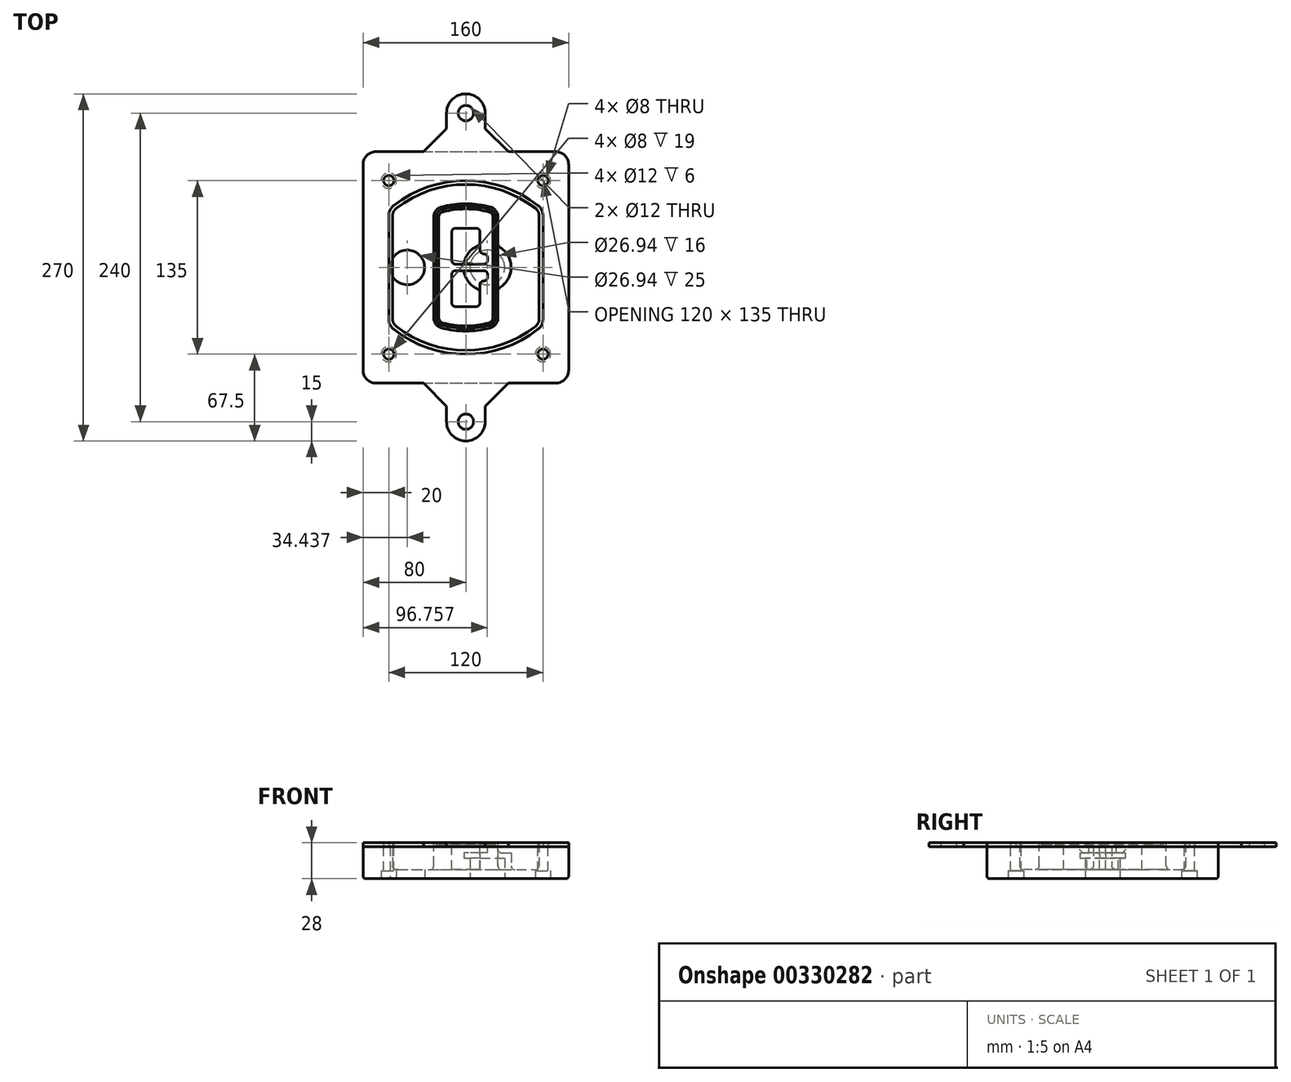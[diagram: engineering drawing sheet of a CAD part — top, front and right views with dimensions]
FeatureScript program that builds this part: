
annotation { "Feature Type Name" : "Feature", "Feature Type Description" : "" }
export const myFeature = defineFeature(function(context is Context, id is Id, definition is map)
    precondition{}
    {
        {
            var Q0;
            Q0=qCreatedBy(makeId("Top.planeOp"),FACE);
            var sketch = newSketch(context, id + "F0", { "sketchPlane" : qUnion([Q0])});
            skPoint(sketch, "E0.rect.middle", {"position": v(0, 0) * mm});
            skLineSegment(sketch, "E1.bottom", {"start": v(-70, -90) * mm, "end": v(70, -90) * mm});
            skLineSegment(sketch, "E1.top", {"start": v(-70, 90) * mm, "end": v(70, 90) * mm});
            skLineSegment(sketch, "E1.left", {"start": v(-80, -80) * mm, "end": v(-80, 80) * mm});
            skLineSegment(sketch, "E1.right", {"start": v(80, -80) * mm, "end": v(80, 80) * mm});
            skLineSegment(sketch, "E2", {"start": v(-80, 90) * mm, "end": v(80, -90) * mm, "construction": true});
            skLineSegment(sketch, "E3", {"start": v(80, 90) * mm, "end": v(-80, -90) * mm, "construction": true});
            skCircle(sketch, "E4", {"center": v(-60, 67.5) * mm, "radius": 4 * mm});
            skCircle(sketch, "E5", {"center": v(60, 67.5) * mm, "radius": 4 * mm});
            skCircle(sketch, "E6", {"center": v(60, -67.5) * mm, "radius": 4 * mm});
            skCircle(sketch, "E7", {"center": v(-60, -67.5) * mm, "radius": 4 * mm});
            skLineSegment(sketch, "E8", {"start": v(-60, 67.5) * mm, "end": v(60, 67.5) * mm, "construction": true});
            skLineSegment(sketch, "E9", {"start": v(60, 67.5) * mm, "end": v(60, -67.5) * mm, "construction": true});
            skLineSegment(sketch, "E10", {"start": v(60, -67.5) * mm, "end": v(-60, -67.5) * mm, "construction": true});
            skLineSegment(sketch, "E11", {"start": v(-60, -67.5) * mm, "end": v(-60, 67.5) * mm, "construction": true});
            skLineSegment(sketch, "E12", {"start": v(-60, 40.3) * mm, "end": v(-60, -40.3) * mm});
            skLineSegment(sketch, "E13", {"start": v(60, 40.3) * mm, "end": v(60, -40.3) * mm});
            skArc(sketch, "E14", {"start": v(56.15, 48.18) * mm, "mid": v(0, 67.5) * mm, "end": v(-56.15, 48.18) * mm});
            skArc(sketch, "E15", {"start": v(-56.15, -48.18) * mm, "mid": v(0, -67.5) * mm, "end": v(56.15, -48.18) * mm});
            skLineSegment(sketch, "E16", {"start": v(-60, 0) * mm, "end": v(60, 0) * mm, "construction": true});
            skPoint(sketch, "E17.visualSharp", {"position": v(-60, -45) * mm});
            skArc(sketch, "E17.filletArc", {"start": v(-60, -40.3) * mm, "mid": v(-58.99, -44.68) * mm, "end": v(-56.15, -48.18) * mm});
            skPoint(sketch, "E18.visualSharp", {"position": v(-60, 45) * mm});
            skArc(sketch, "E18.filletArc", {"start": v(-56.15, 48.18) * mm, "mid": v(-58.99, 44.68) * mm, "end": v(-60, 40.3) * mm});
            skPoint(sketch, "E19.visualSharp", {"position": v(60, 45) * mm});
            skArc(sketch, "E19.filletArc", {"start": v(60, 40.3) * mm, "mid": v(58.99, 44.68) * mm, "end": v(56.15, 48.18) * mm});
            skPoint(sketch, "E20.visualSharp", {"position": v(60, -45) * mm});
            skArc(sketch, "E20.filletArc", {"start": v(56.15, -48.18) * mm, "mid": v(58.99, -44.68) * mm, "end": v(60, -40.3) * mm});
            skPoint(sketch, "E21.visualSharp", {"position": v(-80, 90) * mm});
            skArc(sketch, "E21.filletArc", {"start": v(-70, 90) * mm, "mid": v(-77.07, 87.07) * mm, "end": v(-80, 80) * mm});
            skPoint(sketch, "E22.visualSharp", {"position": v(80, 90) * mm});
            skArc(sketch, "E22.filletArc", {"start": v(80, 80) * mm, "mid": v(77.07, 87.07) * mm, "end": v(70, 90) * mm});
            skPoint(sketch, "E23.visualSharp", {"position": v(80, -90) * mm});
            skArc(sketch, "E23.filletArc", {"start": v(70, -90) * mm, "mid": v(77.07, -87.07) * mm, "end": v(80, -80) * mm});
            skPoint(sketch, "E24.visualSharp", {"position": v(-80, -90) * mm});
            skArc(sketch, "E24.filletArc", {"start": v(-80, -80) * mm, "mid": v(-77.07, -87.07) * mm, "end": v(-70, -90) * mm});
            skArc(sketch, "E25.0", {"start": v(57, 40.3) * mm, "mid": v(56.3, 43.36) * mm, "end": v(54.3, 45.81) * mm});
            skLineSegment(sketch, "E25.1", {"start": v(57, 40.3) * mm, "end": v(57, -40.3) * mm});
            skArc(sketch, "E25.2", {"start": v(54.3, -45.81) * mm, "mid": v(56.3, -43.36) * mm, "end": v(57, -40.3) * mm});
            skArc(sketch, "E25.3", {"start": v(-54.3, -45.81) * mm, "mid": v(0, -64.5) * mm, "end": v(54.3, -45.81) * mm});
            skArc(sketch, "E25.4", {"start": v(-57, -40.3) * mm, "mid": v(-56.3, -43.36) * mm, "end": v(-54.3, -45.81) * mm});
            skArc(sketch, "E25.5", {"start": v(54.3, 45.81) * mm, "mid": v(0, 64.5) * mm, "end": v(-54.3, 45.81) * mm});
            skLineSegment(sketch, "E25.6", {"start": v(-57, 40.3) * mm, "end": v(-57, -40.3) * mm});
            skArc(sketch, "E25.7", {"start": v(-54.3, 45.81) * mm, "mid": v(-56.3, 43.36) * mm, "end": v(-57, 40.3) * mm});
            skArc(sketch, "E26.0", {"start": v(-58.62, 51.33) * mm, "mid": v(-62.58, 46.43) * mm, "end": v(-64, 40.3) * mm});
            skArc(sketch, "E26.1", {"start": v(58.62, 51.33) * mm, "mid": v(0, 71.5) * mm, "end": v(-58.62, 51.33) * mm});
            skArc(sketch, "E26.2", {"start": v(64, 40.3) * mm, "mid": v(62.58, 46.43) * mm, "end": v(58.62, 51.33) * mm});
            skLineSegment(sketch, "E26.3", {"start": v(64, 40.3) * mm, "end": v(64, -40.3) * mm});
            skArc(sketch, "E26.4", {"start": v(58.62, -51.33) * mm, "mid": v(62.58, -46.43) * mm, "end": v(64, -40.3) * mm});
            skLineSegment(sketch, "E26.5", {"start": v(-64, 40.3) * mm, "end": v(-64, -40.3) * mm});
            skArc(sketch, "E26.6", {"start": v(-58.62, -51.33) * mm, "mid": v(0, -71.5) * mm, "end": v(58.62, -51.33) * mm});
            skArc(sketch, "E26.7", {"start": v(-64, -40.3) * mm, "mid": v(-62.58, -46.43) * mm, "end": v(-58.62, -51.33) * mm});
            skSolve(sketch);
        }
        {
            var Q0;
            Q0=makeQuery(id+"F0.imprint","IMPRINT",FACE,{"disambiguationData":[TD([[makeQuery(id+"F0.imprint","IMPRINT",EDGE,{"derivedFrom":sQuery(id+"F0.wireOp",EDGE,"E1.bottom")}),1.0]])]});
            var Q1;
            Q1=makeQuery(id+"F0.imprint","IMPRINT",FACE,{"disambiguationData":[TD([[makeQuery(id+"F0.imprint","IMPRINT",EDGE,{"derivedFrom":sQuery(id+"F0.wireOp",EDGE,"E12")}),1.0]])]});
            var Q2;
            Q2=makeQuery(id+"F0.imprint","IMPRINT",FACE,{"disambiguationData":[TD([[makeQuery(id+"F0.imprint","IMPRINT",EDGE,{"derivedFrom":sQuery(id+"F0.wireOp",EDGE,"E25.0")}),1.0]])]});
            var Q3;
            Q3=makeQuery(id+"F0.imprint","IMPRINT",FACE,{"disambiguationData":[TD([[makeQuery(id+"F0.imprint","IMPRINT",EDGE,{"derivedFrom":sQuery(id+"F0.wireOp",EDGE,"E12")}),-1.0]])]});
            extrude(context, id + "F1", {"entities" : qUnion([Q0, Q1, Q2, Q3]), "oppositeDirection" : true, "depth" : 25 * mm});
        }
        {
            var Q0;
            Q0=makeQuery(id+"F0.imprint","IMPRINT",FACE,{"disambiguationData":[TD([[makeQuery(id+"F0.imprint","IMPRINT",EDGE,{"derivedFrom":sQuery(id+"F0.wireOp",EDGE,"E12")}),1.0]])]});
            extrude(context, id + "F2", {"entities" : qUnion([Q0]), "operationType" : NewBodyOperationType.ADD, "depth" : 3 * mm});
        }
        {
            var Q0;
            Q0=makeQuery(id+"F0.imprint","IMPRINT",FACE,{"disambiguationData":[TD([[makeQuery(id+"F0.imprint","IMPRINT",EDGE,{"derivedFrom":sQuery(id+"F0.wireOp",EDGE,"E25.0")}),1.0]])]});
            extrude(context, id + "F3", {"entities" : qUnion([Q0]), "operationType" : NewBodyOperationType.REMOVE, "oppositeDirection" : true, "depth" : 18 * mm});
        }
        {
            var Q0;
            Q0=makeQuery(id+"F2.opExtrude","CAP_FACE",FACE,{"disambiguationData":[OSD([sQuery(id+"F0.wireOp",EDGE,"E12"),sQuery(id+"F0.wireOp",EDGE,"E13"),sQuery(id+"F0.wireOp",EDGE,"E14"),sQuery(id+"F0.wireOp",EDGE,"E15"),sQuery(id+"F0.wireOp",EDGE,"E17.filletArc"),sQuery(id+"F0.wireOp",EDGE,"E18.filletArc"),sQuery(id+"F0.wireOp",EDGE,"E19.filletArc"),sQuery(id+"F0.wireOp",EDGE,"E20.filletArc"),sQuery(id+"F0.wireOp",EDGE,"E25.0"),sQuery(id+"F0.wireOp",EDGE,"E25.1"),sQuery(id+"F0.wireOp",EDGE,"E25.2"),sQuery(id+"F0.wireOp",EDGE,"E25.3"),sQuery(id+"F0.wireOp",EDGE,"E25.4"),sQuery(id+"F0.wireOp",EDGE,"E25.5"),sQuery(id+"F0.wireOp",EDGE,"E25.6"),sQuery(id+"F0.wireOp",EDGE,"E25.7")])],"isStart":false});
            var sketch = newSketch(context, id + "F4", { "sketchPlane" : qUnion([Q0])});
            skArc(sketch, "E27.0", {"start": v(-19.08, -46.97) * mm, "mid": v(0, -49.5) * mm, "end": v(19.08, -46.97) * mm});
            skArc(sketch, "E28.0", {"start": v(19.08, 46.97) * mm, "mid": v(0, 49.5) * mm, "end": v(-19.08, 46.97) * mm});
            skLineSegment(sketch, "E29", {"start": v(-25, 39.25) * mm, "end": v(-25, -39.25) * mm});
            skLineSegment(sketch, "E30", {"start": v(25, 39.25) * mm, "end": v(25, -39.25) * mm});
            skLineSegment(sketch, "E31", {"start": v(-25, 45.1) * mm, "end": v(25, 45.1) * mm, "construction": true});
            skLineSegment(sketch, "E32", {"start": v(-25, -45.1) * mm, "end": v(25, -45.1) * mm, "construction": true});
            skPoint(sketch, "E33.visualSharp", {"position": v(-25, 45.1) * mm});
            skArc(sketch, "E33.filletArc", {"start": v(-19.08, 46.97) * mm, "mid": v(-23.35, 44.11) * mm, "end": v(-25, 39.25) * mm});
            skPoint(sketch, "E34.visualSharp", {"position": v(25, 45.1) * mm});
            skArc(sketch, "E34.filletArc", {"start": v(25, 39.25) * mm, "mid": v(23.35, 44.11) * mm, "end": v(19.08, 46.97) * mm});
            skPoint(sketch, "E35.visualSharp", {"position": v(25, -45.1) * mm});
            skArc(sketch, "E35.filletArc", {"start": v(19.08, -46.97) * mm, "mid": v(23.35, -44.11) * mm, "end": v(25, -39.25) * mm});
            skPoint(sketch, "E36.visualSharp", {"position": v(-25, -45.1) * mm});
            skArc(sketch, "E36.filletArc", {"start": v(-25, -39.25) * mm, "mid": v(-23.35, -44.11) * mm, "end": v(-19.08, -46.97) * mm});
            skArc(sketch, "E37.0", {"start": v(54.3, 45.81) * mm, "mid": v(0, 64.5) * mm, "end": v(-54.3, 45.81) * mm});
            skArc(sketch, "E37.1", {"start": v(-54.3, 45.81) * mm, "mid": v(-56.3, 43.36) * mm, "end": v(-57, 40.3) * mm});
            skLineSegment(sketch, "E37.2", {"start": v(-57, 40.3) * mm, "end": v(-57, -40.3) * mm});
            skArc(sketch, "E37.3", {"start": v(-57, -40.3) * mm, "mid": v(-56.3, -43.36) * mm, "end": v(-54.3, -45.81) * mm});
            skArc(sketch, "E37.4", {"start": v(-54.3, -45.81) * mm, "mid": v(0, -64.5) * mm, "end": v(54.3, -45.81) * mm});
            skArc(sketch, "E37.5", {"start": v(54.3, -45.81) * mm, "mid": v(56.3, -43.36) * mm, "end": v(57, -40.3) * mm});
            skLineSegment(sketch, "E37.6", {"start": v(57, 40.3) * mm, "end": v(57, -40.3) * mm});
            skArc(sketch, "E37.7", {"start": v(57, 40.3) * mm, "mid": v(56.3, 43.36) * mm, "end": v(54.3, 45.81) * mm});
            skLineSegment(sketch, "E38.0", {"start": v(23, 39.25) * mm, "end": v(23, -39.25) * mm});
            skArc(sketch, "E38.1", {"start": v(18.56, -45.04) * mm, "mid": v(21.76, -42.9) * mm, "end": v(23, -39.25) * mm});
            skArc(sketch, "E38.2", {"start": v(-18.56, -45.04) * mm, "mid": v(0, -47.5) * mm, "end": v(18.56, -45.04) * mm});
            skArc(sketch, "E38.3", {"start": v(-23, -39.25) * mm, "mid": v(-21.76, -42.9) * mm, "end": v(-18.56, -45.04) * mm});
            skLineSegment(sketch, "E38.4", {"start": v(-23, 39.25) * mm, "end": v(-23, -39.25) * mm});
            skArc(sketch, "E38.5", {"start": v(23, 39.25) * mm, "mid": v(21.76, 42.9) * mm, "end": v(18.56, 45.04) * mm});
            skArc(sketch, "E38.6", {"start": v(-18.56, 45.04) * mm, "mid": v(-21.76, 42.9) * mm, "end": v(-23, 39.25) * mm});
            skArc(sketch, "E38.7", {"start": v(18.56, 45.04) * mm, "mid": v(0, 47.5) * mm, "end": v(-18.56, 45.04) * mm});
            skArc(sketch, "E39.0", {"start": v(21, 39.25) * mm, "mid": v(20.18, 41.68) * mm, "end": v(18.04, 43.1) * mm});
            skLineSegment(sketch, "E39.1", {"start": v(21, 39.25) * mm, "end": v(21, -39.25) * mm});
            skArc(sketch, "E39.2", {"start": v(18.04, -43.1) * mm, "mid": v(20.18, -41.68) * mm, "end": v(21, -39.25) * mm});
            skArc(sketch, "E39.3", {"start": v(-18.04, -43.1) * mm, "mid": v(0, -45.5) * mm, "end": v(18.04, -43.1) * mm});
            skArc(sketch, "E39.4", {"start": v(-21, -39.25) * mm, "mid": v(-20.18, -41.68) * mm, "end": v(-18.04, -43.1) * mm});
            skArc(sketch, "E39.5", {"start": v(18.04, 43.1) * mm, "mid": v(0, 45.5) * mm, "end": v(-18.04, 43.1) * mm});
            skLineSegment(sketch, "E39.6", {"start": v(-21, 39.25) * mm, "end": v(-21, -39.25) * mm});
            skArc(sketch, "E39.7", {"start": v(-18.04, 43.1) * mm, "mid": v(-20.18, 41.68) * mm, "end": v(-21, 39.25) * mm});
            skLineSegment(sketch, "E40", {"start": v(-25, 0) * mm, "end": v(25, 0) * mm, "construction": true});
            skLineSegment(sketch, "E41", {"start": v(-11, 5.5) * mm, "end": v(-11, 27.5) * mm});
            skLineSegment(sketch, "E42", {"start": v(-8, 30.5) * mm, "end": v(8, 30.5) * mm});
            skLineSegment(sketch, "E43", {"start": v(11, 27.5) * mm, "end": v(11, 13.5) * mm});
            skLineSegment(sketch, "E44", {"start": v(14, 10.5) * mm, "end": v(14, 10.5) * mm});
            skLineSegment(sketch, "E45", {"start": v(17, 7.5) * mm, "end": v(17, 5.5) * mm});
            skLineSegment(sketch, "E46", {"start": v(14, 2.5) * mm, "end": v(-8, 2.5) * mm});
            skPoint(sketch, "E47.visualSharp", {"position": v(-11, 30.5) * mm});
            skArc(sketch, "E47.filletArc", {"start": v(-8, 30.5) * mm, "mid": v(-10.12, 29.62) * mm, "end": v(-11, 27.5) * mm});
            skPoint(sketch, "E48.visualSharp", {"position": v(11, 30.5) * mm});
            skArc(sketch, "E48.filletArc", {"start": v(11, 27.5) * mm, "mid": v(10.12, 29.62) * mm, "end": v(8, 30.5) * mm});
            skPoint(sketch, "E49.visualSharp", {"position": v(11, 10.5) * mm});
            skArc(sketch, "E49.filletArc", {"start": v(11, 13.5) * mm, "mid": v(11.88, 11.38) * mm, "end": v(14, 10.5) * mm});
            skPoint(sketch, "E50.visualSharp", {"position": v(17, 10.5) * mm});
            skArc(sketch, "E50.filletArc", {"start": v(17, 7.5) * mm, "mid": v(16.12, 9.62) * mm, "end": v(14, 10.5) * mm});
            skPoint(sketch, "E51.visualSharp", {"position": v(17, 2.5) * mm});
            skArc(sketch, "E51.filletArc", {"start": v(14, 2.5) * mm, "mid": v(16.12, 3.38) * mm, "end": v(17, 5.5) * mm});
            skPoint(sketch, "E52.visualSharp", {"position": v(-11, 2.5) * mm});
            skArc(sketch, "E52.filletArc", {"start": v(-11, 5.5) * mm, "mid": v(-10.12, 3.38) * mm, "end": v(-8, 2.5) * mm});
            skLineSegment(sketch, "E53.0.MirrorCS", {"start": v(14, -2.5) * mm, "end": v(-8, -2.5) * mm});
            skArc(sketch, "E54.0.MirrorCS", {"start": v(-11, -5.5) * mm, "mid": v(-10.12, -3.38) * mm, "end": v(-8, -2.5) * mm});
            skLineSegment(sketch, "E55.0.MirrorCS", {"start": v(-11, -5.5) * mm, "end": v(-11, -27.5) * mm});
            skArc(sketch, "E56.0.MirrorCS", {"start": v(-8, -30.5) * mm, "mid": v(-10.12, -29.62) * mm, "end": v(-11, -27.5) * mm});
            skLineSegment(sketch, "E57.0.MirrorCS", {"start": v(-8, -30.5) * mm, "end": v(8, -30.5) * mm});
            skArc(sketch, "E58.0.MirrorCS", {"start": v(11, -27.5) * mm, "mid": v(10.12, -29.62) * mm, "end": v(8, -30.5) * mm});
            skLineSegment(sketch, "E59.0.MirrorCS", {"start": v(11, -27.5) * mm, "end": v(11, -13.5) * mm});
            skArc(sketch, "E60.0.MirrorCS", {"start": v(11, -13.5) * mm, "mid": v(11.88, -11.38) * mm, "end": v(14, -10.5) * mm});
            skArc(sketch, "E61.0.MirrorCS", {"start": v(17, -7.5) * mm, "mid": v(16.12, -9.62) * mm, "end": v(14, -10.5) * mm});
            skLineSegment(sketch, "E62.0.MirrorCS", {"start": v(17, -7.5) * mm, "end": v(17, -5.5) * mm});
            skArc(sketch, "E63.0.MirrorCS", {"start": v(14, -2.5) * mm, "mid": v(16.12, -3.38) * mm, "end": v(17, -5.5) * mm});
            skSolve(sketch);
        }
        {
            var Q0;
            Q0=makeQuery(id+"F4.imprint","IMPRINT",FACE,{"disambiguationData":[TD([[makeQuery(id+"F4.imprint","IMPRINT",EDGE,{"derivedFrom":sQuery(id+"F4.wireOp",EDGE,"E27.0")}),1.0]])]});
            var Q1;
            Q1=makeQuery(id+"F4.imprint","IMPRINT",FACE,{"disambiguationData":[TD([[makeQuery(id+"F4.imprint","IMPRINT",EDGE,{"derivedFrom":sQuery(id+"F4.wireOp",EDGE,"E38.0")}),-1.0]])]});
            var Q2;
            Q2=makeQuery(id+"F4.imprint","IMPRINT",FACE,{"disambiguationData":[TD([[makeQuery(id+"F4.imprint","IMPRINT",EDGE,{"derivedFrom":sQuery(id+"F4.wireOp",EDGE,"E39.0")}),1.0]])]});
            extrude(context, id + "F5", {"entities" : qUnion([Q0, Q1, Q2]), "operationType" : NewBodyOperationType.ADD, "endBound" : BoundingType.UP_TO_NEXT, "oppositeDirection" : true, "depth" : 25 * mm});
        }
        {
            var Q0;
            Q0=makeQuery(id+"F4.imprint","IMPRINT",FACE,{"disambiguationData":[TD([[makeQuery(id+"F4.imprint","IMPRINT",EDGE,{"derivedFrom":sQuery(id+"F4.wireOp",EDGE,"E38.0")}),-1.0]])]});
            extrude(context, id + "F6", {"entities" : qUnion([Q0]), "operationType" : NewBodyOperationType.REMOVE, "oppositeDirection" : true, "depth" : 2 * mm});
        }
        {
            var Q0;
            Q0=makeQuery(id+"F1.opExtrude","CAP_FACE",FACE,{"disambiguationData":[OSD([sQuery(id+"F0.wireOp",EDGE,"E1.bottom"),sQuery(id+"F0.wireOp",EDGE,"E1.top"),sQuery(id+"F0.wireOp",EDGE,"E1.left"),sQuery(id+"F0.wireOp",EDGE,"E1.right"),sQuery(id+"F0.wireOp",EDGE,"E4"),sQuery(id+"F0.wireOp",EDGE,"E5"),sQuery(id+"F0.wireOp",EDGE,"E6"),sQuery(id+"F0.wireOp",EDGE,"E7"),sQuery(id+"F0.wireOp",EDGE,"E21.filletArc"),sQuery(id+"F0.wireOp",EDGE,"E22.filletArc"),sQuery(id+"F0.wireOp",EDGE,"E23.filletArc"),sQuery(id+"F0.wireOp",EDGE,"E24.filletArc")])],"isStart":false});
            var sketch = newSketch(context, id + "F7", { "sketchPlane" : qUnion([Q0])});
            skCircle(sketch, "E64", {"center": v(16.76, 0) * mm, "radius": 13.47 * mm});
            skCircle(sketch, "E65", {"center": v(-45.56, 0) * mm, "radius": 13.47 * mm});
            skLineSegment(sketch, "E66", {"start": v(80, 0) * mm, "end": v(-80, 0) * mm});
            skCircle(sketch, "E67", {"center": v(16.76, 0) * mm, "radius": 18.47 * mm});
            skCircle(sketch, "E68", {"center": v(60, -67.5) * mm, "radius": 6 * mm});
            skCircle(sketch, "E69", {"center": v(-60, -67.5) * mm, "radius": 6 * mm});
            skCircle(sketch, "E70", {"center": v(-60, 67.5) * mm, "radius": 6 * mm});
            skCircle(sketch, "E71", {"center": v(60, 67.5) * mm, "radius": 6 * mm});
            skSolve(sketch);
        }
        {
            var Q0;
            {var subQ1=sQuery(id+"F7.wireOp",EDGE,"E66");var subQ4=sQuery(id+"F7.wireOp",EDGE,"E64");var subQ6=makeQuery(id+"F7.imprint","INTERSECT",VERTEX,{"disambiguationData":[OD(0.0)],"derivedFrom":[subQ4,subQ1]});Q0=makeQuery(id+"F7.imprint","IMPRINT",FACE,{"disambiguationData":[TD([[makeQuery(id+"F7.imprint","IMPRINT",EDGE,{"disambiguationData":[TD([[subQ6,-1.0]])],"derivedFrom":subQ4}),-1.0]])]});}
            var Q1;
            {var subQ0=sQuery(id+"F7.wireOp",EDGE,"E66");var subQ1=sQuery(id+"F7.wireOp",EDGE,"E64");var subQ3=makeQuery(id+"F7.imprint","INTERSECT",VERTEX,{"disambiguationData":[OD(0.0)],"derivedFrom":[subQ1,subQ0]});Q1=makeQuery(id+"F7.imprint","IMPRINT",FACE,{"disambiguationData":[TD([[makeQuery(id+"F7.imprint","IMPRINT",EDGE,{"disambiguationData":[TD([[subQ3,-1.0]])],"derivedFrom":subQ1}),1.0]])]});}
            var Q2;
            {var subQ0=sQuery(id+"F7.wireOp",EDGE,"E66");var subQ1=sQuery(id+"F7.wireOp",EDGE,"E64");var subQ3=makeQuery(id+"F7.imprint","INTERSECT",VERTEX,{"disambiguationData":[OD(0.0)],"derivedFrom":[subQ1,subQ0]});Q2=makeQuery(id+"F7.imprint","IMPRINT",FACE,{"disambiguationData":[TD([[makeQuery(id+"F7.imprint","IMPRINT",EDGE,{"disambiguationData":[TD([[subQ3,1.0]])],"derivedFrom":subQ1}),1.0]])]});}
            var Q3;
            {var subQ1=sQuery(id+"F7.wireOp",EDGE,"E66");var subQ4=sQuery(id+"F7.wireOp",EDGE,"E64");var subQ6=makeQuery(id+"F7.imprint","INTERSECT",VERTEX,{"disambiguationData":[OD(0.0)],"derivedFrom":[subQ4,subQ1]});Q3=makeQuery(id+"F7.imprint","IMPRINT",FACE,{"disambiguationData":[TD([[makeQuery(id+"F7.imprint","IMPRINT",EDGE,{"disambiguationData":[TD([[subQ6,1.0]])],"derivedFrom":subQ4}),-1.0]])]});}
            extrude(context, id + "F8", {"entities" : qUnion([Q0, Q1, Q2, Q3]), "operationType" : NewBodyOperationType.ADD, "oppositeDirection" : true, "depth" : 20 * mm});
        }
        {
            var Q0;
            {var subQ0=sQuery(id+"F7.wireOp",EDGE,"E66");var subQ1=sQuery(id+"F7.wireOp",EDGE,"E64");var subQ3=makeQuery(id+"F7.imprint","INTERSECT",VERTEX,{"disambiguationData":[OD(0.0)],"derivedFrom":[subQ1,subQ0]});Q0=makeQuery(id+"F7.imprint","IMPRINT",FACE,{"disambiguationData":[TD([[makeQuery(id+"F7.imprint","IMPRINT",EDGE,{"disambiguationData":[TD([[subQ3,-1.0]])],"derivedFrom":subQ1}),1.0]])]});}
            var Q1;
            {var subQ0=sQuery(id+"F7.wireOp",EDGE,"E66");var subQ1=sQuery(id+"F7.wireOp",EDGE,"E64");var subQ3=makeQuery(id+"F7.imprint","INTERSECT",VERTEX,{"disambiguationData":[OD(0.0)],"derivedFrom":[subQ1,subQ0]});Q1=makeQuery(id+"F7.imprint","IMPRINT",FACE,{"disambiguationData":[TD([[makeQuery(id+"F7.imprint","IMPRINT",EDGE,{"disambiguationData":[TD([[subQ3,1.0]])],"derivedFrom":subQ1}),1.0]])]});}
            extrude(context, id + "F9", {"entities" : qUnion([Q0, Q1]), "operationType" : NewBodyOperationType.REMOVE, "oppositeDirection" : true, "depth" : 16 * mm});
        }
        {
            var Q0;
            {var subQ0=sQuery(id+"F7.wireOp",EDGE,"E66");var subQ1=sQuery(id+"F7.wireOp",EDGE,"E65");var subQ3=makeQuery(id+"F7.imprint","INTERSECT",VERTEX,{"disambiguationData":[OD(0.0)],"derivedFrom":[subQ1,subQ0]});Q0=makeQuery(id+"F7.imprint","IMPRINT",FACE,{"disambiguationData":[TD([[makeQuery(id+"F7.imprint","IMPRINT",EDGE,{"disambiguationData":[TD([[subQ3,-1.0]])],"derivedFrom":subQ1}),1.0]])]});}
            var Q1;
            {var subQ0=sQuery(id+"F7.wireOp",EDGE,"E66");var subQ1=sQuery(id+"F7.wireOp",EDGE,"E65");var subQ3=makeQuery(id+"F7.imprint","INTERSECT",VERTEX,{"disambiguationData":[OD(0.0)],"derivedFrom":[subQ1,subQ0]});Q1=makeQuery(id+"F7.imprint","IMPRINT",FACE,{"disambiguationData":[TD([[makeQuery(id+"F7.imprint","IMPRINT",EDGE,{"disambiguationData":[TD([[subQ3,1.0]])],"derivedFrom":subQ1}),1.0]])]});}
            extrude(context, id + "F10", {"entities" : qUnion([Q0, Q1]), "operationType" : NewBodyOperationType.REMOVE, "oppositeDirection" : true, "depth" : 25 * mm});
        }
        {
            var Q0;
            Q0=makeQuery(id+"F7.imprint","IMPRINT",FACE,{"disambiguationData":[TD([[makeQuery(id+"F7.imprint","IMPRINT",EDGE,{"derivedFrom":sQuery(id+"F7.wireOp",EDGE,"E68")}),1.0]])]});
            var Q1;
            Q1=makeQuery(id+"F7.imprint","IMPRINT",FACE,{"disambiguationData":[TD([[makeQuery(id+"F7.imprint","IMPRINT",EDGE,{"derivedFrom":makeQuery(id+"F1.opExtrude","CAP_EDGE",EDGE,{"disambiguationData":[OSD([sQuery(id+"F0.wireOp",EDGE,"E5")])],"isStart":false})}),-1.0]])]});
            var Q2;
            Q2=makeQuery(id+"F7.imprint","IMPRINT",FACE,{"disambiguationData":[TD([[makeQuery(id+"F7.imprint","IMPRINT",EDGE,{"derivedFrom":sQuery(id+"F7.wireOp",EDGE,"E69")}),1.0]])]});
            var Q3;
            Q3=makeQuery(id+"F7.imprint","IMPRINT",FACE,{"disambiguationData":[TD([[makeQuery(id+"F7.imprint","IMPRINT",EDGE,{"derivedFrom":makeQuery(id+"F1.opExtrude","CAP_EDGE",EDGE,{"disambiguationData":[OSD([sQuery(id+"F0.wireOp",EDGE,"E4")])],"isStart":false})}),-1.0]])]});
            var Q4;
            Q4=makeQuery(id+"F7.imprint","IMPRINT",FACE,{"disambiguationData":[TD([[makeQuery(id+"F7.imprint","IMPRINT",EDGE,{"derivedFrom":sQuery(id+"F7.wireOp",EDGE,"E70")}),1.0]])]});
            var Q5;
            Q5=makeQuery(id+"F7.imprint","IMPRINT",FACE,{"disambiguationData":[TD([[makeQuery(id+"F7.imprint","IMPRINT",EDGE,{"derivedFrom":makeQuery(id+"F1.opExtrude","CAP_EDGE",EDGE,{"disambiguationData":[OSD([sQuery(id+"F0.wireOp",EDGE,"E7")])],"isStart":false})}),-1.0]])]});
            var Q6;
            Q6=makeQuery(id+"F7.imprint","IMPRINT",FACE,{"disambiguationData":[TD([[makeQuery(id+"F7.imprint","IMPRINT",EDGE,{"derivedFrom":sQuery(id+"F7.wireOp",EDGE,"E71")}),1.0]])]});
            var Q7;
            Q7=makeQuery(id+"F7.imprint","IMPRINT",FACE,{"disambiguationData":[TD([[makeQuery(id+"F7.imprint","IMPRINT",EDGE,{"derivedFrom":makeQuery(id+"F1.opExtrude","CAP_EDGE",EDGE,{"disambiguationData":[OSD([sQuery(id+"F0.wireOp",EDGE,"E6")])],"isStart":false})}),-1.0]])]});
            extrude(context, id + "F11", {"entities" : qUnion([Q0, Q1, Q2, Q3, Q4, Q5, Q6, Q7]), "operationType" : NewBodyOperationType.REMOVE, "oppositeDirection" : true, "depth" : 6 * mm});
        }
        {
            var Q0;
            Q0=makeQuery(id+"F9.boolean.opBoolean","COPY",FACE,{"derivedFrom":makeQuery(id+"F9.opExtrude","CAP_FACE",FACE,{"disambiguationData":[OSD([sQuery(id+"F7.wireOp",EDGE,"E64")])],"isStart":false})});
            var sketch = newSketch(context, id + "F12", { "sketchPlane" : qUnion([Q0])});
            skArc(sketch, "E72.0", {"start": v(11, 17.55) * mm, "mid": v(2.57, 11.82) * mm, "end": v(-1.54, 2.5) * mm});
            skArc(sketch, "E72.1", {"start": v(-1.54, -2.5) * mm, "mid": v(2.57, -11.82) * mm, "end": v(11, -17.55) * mm});
            skLineSegment(sketch, "E73", {"start": v(-1.54, -2.5) * mm, "end": v(14, -2.5) * mm});
            skLineSegment(sketch, "E74.0", {"start": v(14, 2.5) * mm, "end": v(-1.54, 2.5) * mm});
            skArc(sketch, "E74.1", {"start": v(14, 2.5) * mm, "mid": v(16.12, 3.38) * mm, "end": v(17, 5.5) * mm});
            skLineSegment(sketch, "E74.2", {"start": v(17, 7.5) * mm, "end": v(17, 5.5) * mm});
            skArc(sketch, "E74.3", {"start": v(17, 7.5) * mm, "mid": v(16.12, 9.62) * mm, "end": v(14, 10.5) * mm});
            skArc(sketch, "E74.4", {"start": v(11, 13.5) * mm, "mid": v(11.88, 11.38) * mm, "end": v(14, 10.5) * mm});
            skLineSegment(sketch, "E74.5", {"start": v(11, 17.55) * mm, "end": v(11, 13.5) * mm});
            skLineSegment(sketch, "E74.7", {"start": v(14, -2.5) * mm, "end": v(-1.54, -2.5) * mm});
            skArc(sketch, "E74.8", {"start": v(14, -2.5) * mm, "mid": v(16.12, -3.38) * mm, "end": v(17, -5.5) * mm});
            skLineSegment(sketch, "E74.9", {"start": v(17, -7.5) * mm, "end": v(17, -5.5) * mm});
            skArc(sketch, "E74.10", {"start": v(17, -7.5) * mm, "mid": v(16.12, -9.62) * mm, "end": v(14, -10.5) * mm});
            skArc(sketch, "E74.11", {"start": v(11, -13.5) * mm, "mid": v(11.88, -11.38) * mm, "end": v(14, -10.5) * mm});
            skLineSegment(sketch, "E74.12", {"start": v(11, -17.55) * mm, "end": v(11, -13.5) * mm});
            skPoint(sketch, "E75.orphan", {"position": v(11, -27.5) * mm});
            skPoint(sketch, "E76.orphan", {"position": v(-8, -2.5) * mm});
            skPoint(sketch, "E77.orphan", {"position": v(-8, 2.5) * mm});
            skPoint(sketch, "E78.orphan", {"position": v(11, 27.5) * mm});
            skSolve(sketch);
        }
        {
            var Q0;
            {var subQ7=sQuery(id+"F12.wireOp",EDGE,"E72.0");var subQ14=sQuery(id+"F12.wireOp",EDGE,"E72.1");var subQ16=sQuery(id+"F12.wireOp",EDGE,"E74.1");var subQ18=sQuery(id+"F12.wireOp",EDGE,"E74.8");Q0=qUnion([makeQuery(id+"F12.imprint","IMPRINT",FACE,{"disambiguationData":[TD([[makeQuery(id+"F12.imprint","IMPRINT",EDGE,{"derivedFrom":subQ7}),1.0]])]}),makeQuery(id+"F12.imprint","IMPRINT",FACE,{"disambiguationData":[TD([[makeQuery(id+"F12.imprint","IMPRINT",EDGE,{"derivedFrom":subQ14}),1.0]])]}),makeQuery(id+"F12.imprint","IMPRINT",FACE,{"disambiguationData":[TD([[makeQuery(id+"F12.imprint","IMPRINT",EDGE,{"derivedFrom":subQ16}),1.0]])]}),makeQuery(id+"F12.imprint","IMPRINT",FACE,{"disambiguationData":[TD([[makeQuery(id+"F12.imprint","IMPRINT",EDGE,{"derivedFrom":subQ18}),-1.0]])]})]);}
            var Q1;
            Q1=makeQuery(id+"F5.boolean.opBoolean","SPLIT",FACE,{"disambiguationData":[TD([makeQuery(id+"F5.opExtrude","SWEPT_FACE",FACE,{"disambiguationData":[OSD([sQuery(id+"F4.wireOp",EDGE,"E41")])]})])],"derivedFrom":makeQuery(id+"F3.boolean.opBoolean","COPY",FACE,{"derivedFrom":makeQuery(id+"F3.opExtrude","CAP_FACE",FACE,{"disambiguationData":[OSD([sQuery(id+"F0.wireOp",EDGE,"E25.0"),sQuery(id+"F0.wireOp",EDGE,"E25.1"),sQuery(id+"F0.wireOp",EDGE,"E25.2"),sQuery(id+"F0.wireOp",EDGE,"E25.3"),sQuery(id+"F0.wireOp",EDGE,"E25.4"),sQuery(id+"F0.wireOp",EDGE,"E25.5"),sQuery(id+"F0.wireOp",EDGE,"E25.6"),sQuery(id+"F0.wireOp",EDGE,"E25.7")])],"isStart":false})})});
            extrude(context, id + "F13", {"entities" : qUnion([Q0]), "operationType" : NewBodyOperationType.REMOVE, "endBound" : BoundingType.UP_TO_SURFACE, "endBoundEntityFace" : qUnion([Q1]), "depth" : 25 * mm});
        }
        {
            var Q0;
            Q0=makeQuery(id+"F3.boolean.opBoolean","COPY",EDGE,{"derivedFrom":makeQuery(id+"F3.opExtrude","CAP_EDGE",EDGE,{"disambiguationData":[OSD([sQuery(id+"F0.wireOp",EDGE,"E25.6")])],"isStart":false})});
            var Q1;
            Q1=makeQuery(id+"F8.boolean.opBoolean","INTERSECT",EDGE,{"derivedFrom":[makeQuery(id+"F5.opExtrude","SWEPT_FACE",FACE,{"disambiguationData":[OSD([sQuery(id+"F4.wireOp",EDGE,"E30")])]}),makeQuery(id+"F8.opExtrude","CAP_FACE",FACE,{"disambiguationData":[OSD([sQuery(id+"F7.wireOp",EDGE,"E67")])],"isStart":false})]});
            var Q2;
            Q2=makeQuery(id+"F8.boolean.opBoolean","INTERSECT",EDGE,{"disambiguationData":[OD(1.0)],"derivedFrom":[makeQuery(id+"F5.opExtrude","SWEPT_FACE",FACE,{"disambiguationData":[OSD([sQuery(id+"F4.wireOp",EDGE,"E30")])]}),makeQuery(id+"F8.opExtrude","SWEPT_FACE",FACE,{"disambiguationData":[OSD([sQuery(id+"F7.wireOp",EDGE,"E67")])]})]});
            var Q3;
            {var subQ0=sQuery(id+"F4.wireOp",EDGE,"E30");Q3=makeQuery(id+"F8.boolean.opBoolean","SPLIT",EDGE,{"disambiguationData":[TD([makeQuery(id+"F5.opExtrude","SWEPT_FACE",FACE,{"disambiguationData":[OSD([sQuery(id+"F4.wireOp",EDGE,"E35.filletArc")])]})])],"derivedFrom":makeQuery(id+"F5.opExtrude","CAP_EDGE",EDGE,{"disambiguationData":[OSD([subQ0])],"isStart":false})});}
            var Q4;
            {var subQ0=sQuery(id+"F0.wireOp",EDGE,"E25.7");var subQ1=sQuery(id+"F0.wireOp",EDGE,"E25.1");var subQ2=sQuery(id+"F0.wireOp",EDGE,"E25.6");var subQ3=sQuery(id+"F0.wireOp",EDGE,"E25.5");var subQ4=sQuery(id+"F0.wireOp",EDGE,"E25.4");var subQ5=sQuery(id+"F0.wireOp",EDGE,"E25.0");var subQ6=sQuery(id+"F0.wireOp",EDGE,"E25.2");var subQ7=sQuery(id+"F0.wireOp",EDGE,"E25.3");Q4=makeQuery(id+"F8.boolean.opBoolean","INTERSECT",EDGE,{"derivedFrom":[makeQuery(id+"F5.boolean.opBoolean","SPLIT",FACE,{"disambiguationData":[TD([makeQuery(id+"F2.opExtrude","SWEPT_FACE",FACE,{"disambiguationData":[OSD([subQ5])]})])],"derivedFrom":makeQuery(id+"F3.boolean.opBoolean","COPY",FACE,{"derivedFrom":makeQuery(id+"F3.opExtrude","CAP_FACE",FACE,{"disambiguationData":[OSD([subQ5,subQ1,subQ6,subQ7,subQ4,subQ3,subQ2,subQ0])],"isStart":false})})}),makeQuery(id+"F8.opExtrude","SWEPT_FACE",FACE,{"disambiguationData":[OSD([sQuery(id+"F7.wireOp",EDGE,"E67")])]})]});}
            var Q5;
            Q5=makeQuery(id+"F8.boolean.opBoolean","INTERSECT",EDGE,{"disambiguationData":[OD(0.0)],"derivedFrom":[makeQuery(id+"F5.opExtrude","SWEPT_FACE",FACE,{"disambiguationData":[OSD([sQuery(id+"F4.wireOp",EDGE,"E30")])]}),makeQuery(id+"F8.opExtrude","SWEPT_FACE",FACE,{"disambiguationData":[OSD([sQuery(id+"F7.wireOp",EDGE,"E67")])]})]});
            fillet(context, id + "F14", {"entities" : qUnion([Q0, Q1, Q2, Q3, Q4, Q5]), "radius" : 3 * mm, "tangentPropagation" : true, "allowEdgeOverflow" : false});
        }
        {
            var Q0;
            Q0=makeQuery(id+"F1.opExtrude","CAP_EDGE",EDGE,{"disambiguationData":[OSD([sQuery(id+"F0.wireOp",EDGE,"E1.bottom")])],"isStart":false});
            fillet(context, id + "F15", {"entities" : qUnion([Q0]), "radius" : 2 * mm, "tangentPropagation" : true, "allowEdgeOverflow" : false});
        }
        {
            var Q0;
            {var subQ0=sQuery(id+"F0.wireOp",EDGE,"E21.filletArc");var subQ1=sQuery(id+"F0.wireOp",EDGE,"E7");var subQ2=sQuery(id+"F0.wireOp",EDGE,"E6");var subQ3=sQuery(id+"F0.wireOp",EDGE,"E5");var subQ4=sQuery(id+"F0.wireOp",EDGE,"E4");var subQ5=sQuery(id+"F0.wireOp",EDGE,"E22.filletArc");var subQ6=sQuery(id+"F0.wireOp",EDGE,"E1.bottom");var subQ7=sQuery(id+"F0.wireOp",EDGE,"E1.right");var subQ8=sQuery(id+"F0.wireOp",EDGE,"E1.top");var subQ9=sQuery(id+"F0.wireOp",EDGE,"E1.left");var subQ10=sQuery(id+"F0.wireOp",EDGE,"E23.filletArc");var subQ11=sQuery(id+"F0.wireOp",EDGE,"E24.filletArc");Q0=makeQuery(id+"F2.boolean.opBoolean","SPLIT",FACE,{"disambiguationData":[TD([makeQuery(id+"F1.opExtrude","SWEPT_FACE",FACE,{"disambiguationData":[OSD([subQ6])]})])],"derivedFrom":makeQuery(id+"F1.opExtrude","CAP_FACE",FACE,{"disambiguationData":[OSD([subQ6,subQ8,subQ9,subQ7,subQ4,subQ3,subQ2,subQ1,subQ0,subQ5,subQ10,subQ11])],"isStart":true})});}
            var sketch = newSketch(context, id + "F16", { "sketchPlane" : qUnion([Q0])});
            skLineSegment(sketch, "E79.0", {"start": v(-80, -80) * mm, "end": v(-80, 80) * mm});
            skLineSegment(sketch, "E80.0", {"start": v(-70, 90) * mm, "end": v(70, 90) * mm});
            skArc(sketch, "E81.0", {"start": v(-70, 90) * mm, "mid": v(-77.07, 87.07) * mm, "end": v(-80, 80) * mm});
            skCircle(sketch, "E81.2", {"center": v(-60, 67.5) * mm, "radius": 4 * mm});
            skCircle(sketch, "E81.4", {"center": v(60, 67.5) * mm, "radius": 4 * mm});
            skArc(sketch, "E81.5", {"start": v(80, 80) * mm, "mid": v(77.07, 87.07) * mm, "end": v(70, 90) * mm});
            skLineSegment(sketch, "E81.6", {"start": v(80, -80) * mm, "end": v(80, 80) * mm});
            skCircle(sketch, "E81.7", {"center": v(60, -67.5) * mm, "radius": 4 * mm});
            skArc(sketch, "E81.8", {"start": v(70, -90) * mm, "mid": v(77.07, -87.07) * mm, "end": v(80, -80) * mm});
            skLineSegment(sketch, "E81.9", {"start": v(-70, -90) * mm, "end": v(70, -90) * mm});
            skArc(sketch, "E81.10", {"start": v(-80, -80) * mm, "mid": v(-77.07, -87.07) * mm, "end": v(-70, -90) * mm});
            skCircle(sketch, "E81.11", {"center": v(-60, -67.5) * mm, "radius": 4 * mm});
            skArc(sketch, "E81.12", {"start": v(56.15, 48.18) * mm, "mid": v(0, 67.5) * mm, "end": v(-56.15, 48.18) * mm});
            skLineSegment(sketch, "E81.13", {"start": v(60, 40.3) * mm, "end": v(60, -40.3) * mm});
            skArc(sketch, "E81.14", {"start": v(-56.15, -48.18) * mm, "mid": v(0, -67.5) * mm, "end": v(56.15, -48.18) * mm});
            skLineSegment(sketch, "E81.15", {"start": v(-60, 40.3) * mm, "end": v(-60, -40.3) * mm});
            skArc(sketch, "E81.16", {"start": v(-60, -40.3) * mm, "mid": v(-58.99, -44.68) * mm, "end": v(-56.15, -48.18) * mm});
            skArc(sketch, "E81.17", {"start": v(-56.15, 48.18) * mm, "mid": v(-58.99, 44.68) * mm, "end": v(-60, 40.3) * mm});
            skArc(sketch, "E81.18", {"start": v(60, 40.3) * mm, "mid": v(58.99, 44.68) * mm, "end": v(56.15, 48.18) * mm});
            skPoint(sketch, "E81.19", {"position": v(60, -40.3) * mm});
            skArc(sketch, "E81.20", {"start": v(56.15, -48.18) * mm, "mid": v(58.99, -44.68) * mm, "end": v(60, -40.3) * mm});
            skLineSegment(sketch, "E82", {"start": v(0, 90) * mm, "end": v(0, 120) * mm, "construction": true});
            skCircle(sketch, "E83", {"center": v(0, 120) * mm, "radius": 6 * mm});
            skArc(sketch, "E84", {"start": v(15, 120) * mm, "mid": v(0, 135) * mm, "end": v(-15, 120) * mm});
            skLineSegment(sketch, "E85", {"start": v(-15, 120) * mm, "end": v(-15, 108) * mm});
            skLineSegment(sketch, "E86", {"start": v(15, 120) * mm, "end": v(15, 108) * mm});
            skLineSegment(sketch, "E87", {"start": v(15, 108) * mm, "end": v(33, 90) * mm});
            skLineSegment(sketch, "E88", {"start": v(-15, 108) * mm, "end": v(-33, 90) * mm});
            skLineSegment(sketch, "E89", {"start": v(-80, 0) * mm, "end": v(80, 0) * mm, "construction": true});
            skLineSegment(sketch, "E90.MirrorCS", {"start": v(-15, -108) * mm, "end": v(-33, -90) * mm});
            skLineSegment(sketch, "E91.MirrorCS", {"start": v(-15, -120) * mm, "end": v(-15, -108) * mm});
            skArc(sketch, "E92.MirrorCS", {"start": v(15, -120) * mm, "mid": v(0, -135) * mm, "end": v(-15, -120) * mm});
            skLineSegment(sketch, "E93.MirrorCS", {"start": v(15, -120) * mm, "end": v(15, -108) * mm});
            skLineSegment(sketch, "E94.MirrorCS", {"start": v(15, -108) * mm, "end": v(33, -90) * mm});
            skCircle(sketch, "E95.MirrorC", {"center": v(0, -120) * mm, "radius": 6 * mm});
            skLineSegment(sketch, "E96.MirrorCS", {"start": v(0, -90) * mm, "end": v(0, -120) * mm, "construction": true});
            skSolve(sketch);
        }
        {
            var Q0;
            {var subQ0=sQuery(id+"F16.wireOp",EDGE,"E90.MirrorCS");Q0=makeQuery(id+"F16.imprint","IMPRINT",FACE,{"disambiguationData":[TD([[makeQuery(id+"F16.imprint","IMPRINT",EDGE,{"derivedFrom":subQ0}),-1.0]])]});}
            var Q1;
            Q1=makeQuery(id+"F16.imprint","IMPRINT",FACE,{"disambiguationData":[TD([[makeQuery(id+"F16.imprint","IMPRINT",EDGE,{"derivedFrom":sQuery(id+"F16.wireOp",EDGE,"E79.0")}),-1.0]])]});
            var Q2;
            Q2=makeQuery(id+"F16.imprint","IMPRINT",FACE,{"disambiguationData":[TD([[makeQuery(id+"F16.imprint","IMPRINT",EDGE,{"derivedFrom":sQuery(id+"F16.wireOp",EDGE,"E83")}),-1.0]])]});
            var Q3;
            Q3=makeQuery(id+"F2.opExtrude","CAP_FACE",FACE,{"disambiguationData":[OSD([sQuery(id+"F0.wireOp",EDGE,"E12"),sQuery(id+"F0.wireOp",EDGE,"E13"),sQuery(id+"F0.wireOp",EDGE,"E14"),sQuery(id+"F0.wireOp",EDGE,"E15"),sQuery(id+"F0.wireOp",EDGE,"E17.filletArc"),sQuery(id+"F0.wireOp",EDGE,"E18.filletArc"),sQuery(id+"F0.wireOp",EDGE,"E19.filletArc"),sQuery(id+"F0.wireOp",EDGE,"E20.filletArc"),sQuery(id+"F0.wireOp",EDGE,"E25.0"),sQuery(id+"F0.wireOp",EDGE,"E25.1"),sQuery(id+"F0.wireOp",EDGE,"E25.2"),sQuery(id+"F0.wireOp",EDGE,"E25.3"),sQuery(id+"F0.wireOp",EDGE,"E25.4"),sQuery(id+"F0.wireOp",EDGE,"E25.5"),sQuery(id+"F0.wireOp",EDGE,"E25.6"),sQuery(id+"F0.wireOp",EDGE,"E25.7")])],"isStart":false});
            extrude(context, id + "F17", {"entities" : qUnion([Q0, Q1, Q2]), "endBound" : BoundingType.UP_TO_SURFACE, "endBoundEntityFace" : qUnion([Q3]), "depth" : 25 * mm});
        }
    });
